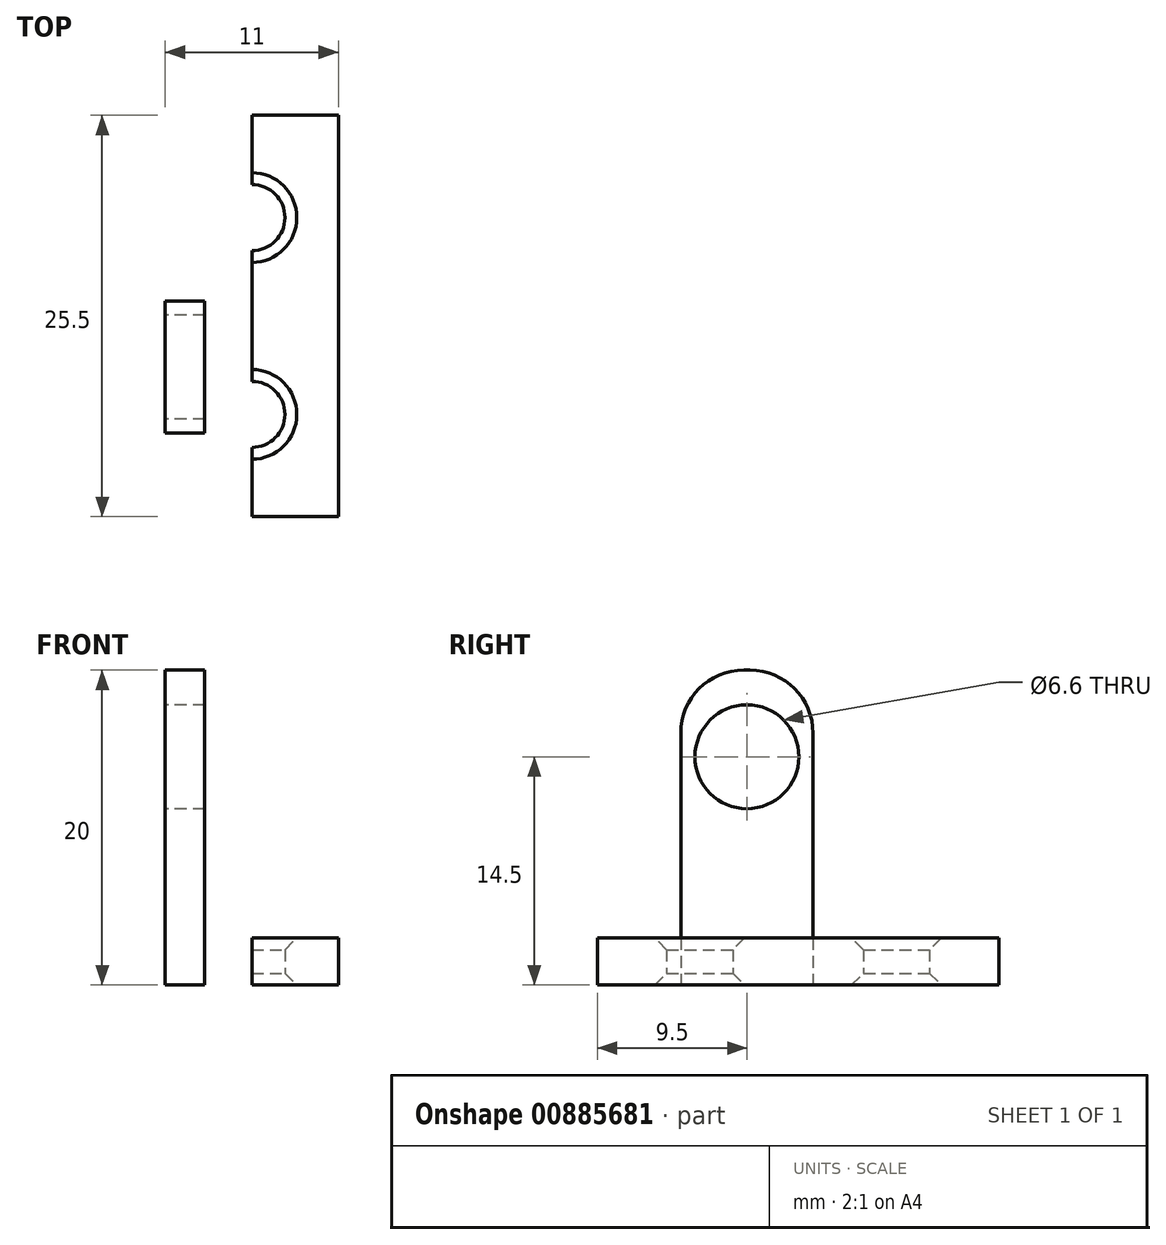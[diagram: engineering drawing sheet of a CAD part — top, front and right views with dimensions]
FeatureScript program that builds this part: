
annotation { "Feature Type Name" : "Feature", "Feature Type Description" : "" }
export const myFeature = defineFeature(function(context is Context, id is Id, definition is map)
    precondition{}
    {
        {
            var Q0;
            Q0=qCreatedBy(makeId("Top.planeOp"),FACE);
            var sketch = newSketch(context, id + "F0", { "sketchPlane" : qUnion([Q0])});
            skLineSegment(sketch, "E0.bottom", {"start": v(0, 0) * mm, "end": v(11, 0) * mm});
            skLineSegment(sketch, "E0.top", {"start": v(0, 25.5) * mm, "end": v(11, 25.5) * mm});
            skLineSegment(sketch, "E0.left", {"start": v(0, 0) * mm, "end": v(0, 25.5) * mm});
            skLineSegment(sketch, "E0.right", {"start": v(11, 0) * mm, "end": v(11, 25.5) * mm});
            skLineSegment(sketch, "E1", {"start": v(5.5, 0) * mm, "end": v(5.5, 25.5) * mm});
            skLineSegment(sketch, "E2", {"start": v(5.5, 0) * mm, "end": v(5.5, 6.5) * mm});
            skLineSegment(sketch, "E3", {"start": v(11, 12.75) * mm, "end": v(14.14, 12.75) * mm});
            skCircle(sketch, "E4", {"center": v(5.5, 6.5) * mm, "radius": 2.1 * mm});
            skCircle(sketch, "E5.MirrorC", {"center": v(5.5, 19) * mm, "radius": 2.1 * mm});
            skLineSegment(sketch, "E6", {"start": v(0, 0) * mm, "end": v(0, 9.5) * mm});
            skLineSegment(sketch, "E7", {"start": v(0, 9.5) * mm, "end": v(0, 5.3) * mm});
            skLineSegment(sketch, "E8", {"start": v(0, 9.5) * mm, "end": v(-2.03, 9.5) * mm});
            skLineSegment(sketch, "E9.MirrorCS", {"start": v(0, 9.5) * mm, "end": v(0, 13.7) * mm});
            skLineSegment(sketch, "E10", {"start": v(0, 5.3) * mm, "end": v(2.5, 5.3) * mm});
            skLineSegment(sketch, "E11.bottom", {"start": v(0, 13.7) * mm, "end": v(2.5, 13.7) * mm});
            skLineSegment(sketch, "E11.left", {"start": v(0, 13.7) * mm, "end": v(0, 5.3) * mm});
            skLineSegment(sketch, "E11.right", {"start": v(2.5, 13.7) * mm, "end": v(2.5, 5.3) * mm});
            skSolve(sketch);
        }
        {
            var Q0;
            {var subQ0=sQuery(id+"F0.wireOp",EDGE,"E0.right");var subQ3=makeQuery(id+"F0.imprint","IMPRINT",VERTEX,{"derivedFrom":subQ0});Q0=makeQuery(id+"F0.imprint","IMPRINT",FACE,{"disambiguationData":[TD([[makeQuery(id+"F0.imprint","IMPRINT",EDGE,{"disambiguationData":[TD([[subQ3,1.0]])],"derivedFrom":subQ0}),1.0]])]});}
            var Q1;
            {var subQ5=sQuery(id+"F0.wireOp",EDGE,"E0.left");Q1=makeQuery(id+"F0.imprint","IMPRINT",FACE,{"disambiguationData":[TD([[makeQuery(id+"F0.imprint","IMPRINT",EDGE,{"derivedFrom":subQ5}),-1.0]])]});}
            extrude(context, id + "F1", {"entities" : qUnion([Q0, Q1]), "depth" : 3 * mm, "offsetDistance" : 25 * mm});
        }
        {
            var Q0;
            {var subQ3=sQuery(id+"F0.wireOp",EDGE,"E11.bottom");Q0=makeQuery(id+"F0.imprint","IMPRINT",FACE,{"disambiguationData":[TD([[makeQuery(id+"F0.imprint","IMPRINT",EDGE,{"derivedFrom":subQ3}),-1.0]])]});}
            extrude(context, id + "F2", {"entities" : qUnion([Q0]), "operationType" : NewBodyOperationType.ADD, "depth" : 20 * mm, "offsetDistance" : 25 * mm});
        }
        {
            var Q0;
            Q0=qCreatedBy(makeId("Right.planeOp"),FACE);
            var sketch = newSketch(context, id + "F3", { "sketchPlane" : qUnion([Q0])});
            skLineSegment(sketch, "E12", {"start": v(0, 0) * mm, "end": v(9.5, 0) * mm});
            skLineSegment(sketch, "E13", {"start": v(9.5, 0) * mm, "end": v(9.5, 14.5) * mm});
            skCircle(sketch, "E14", {"center": v(9.5, 14.5) * mm, "radius": 3.3 * mm});
            skSolve(sketch);
        }
        {
            var Q0;
            Q0=makeQuery(id+"F3.imprint","IMPRINT",FACE,{"disambiguationData":[TD([[makeQuery(id+"F3.imprint","IMPRINT",EDGE,{"derivedFrom":sQuery(id+"F3.wireOp",EDGE,"E14")}),1.0]])]});
            extrude(context, id + "F4", {"entities" : qUnion([Q0]), "operationType" : NewBodyOperationType.REMOVE, "depth" : 25 * mm, "offsetDistance" : 25 * mm});
        }
        {
            var Q0;
            Q0=makeQuery(id+"F2.opExtrude","CAP_EDGE",EDGE,{"disambiguationData":[OSD([sQuery(id+"F0.wireOp",EDGE,"E10")])],"isStart":false});
            var Q1;
            Q1=makeQuery(id+"F2.opExtrude","CAP_EDGE",EDGE,{"disambiguationData":[OSD([sQuery(id+"F0.wireOp",EDGE,"E11.bottom")])],"isStart":false});
            fillet(context, id + "F5", {"entities" : qUnion([Q0, Q1]), "radius" : 4 * mm, "tangentPropagation" : true, "allowEdgeOverflow" : false});
        }
        {
            var Q0;
            Q0=makeQuery(id+"F1.opExtrude","CAP_EDGE",EDGE,{"disambiguationData":[OSD([sQuery(id+"F0.wireOp",EDGE,"E5.MirrorC")])],"isStart":false});
            var Q1;
            Q1=makeQuery(id+"F1.opExtrude","CAP_EDGE",EDGE,{"disambiguationData":[OSD([sQuery(id+"F0.wireOp",EDGE,"E5.MirrorC")])],"isStart":true});
            var Q2;
            Q2=makeQuery(id+"F1.opExtrude","CAP_EDGE",EDGE,{"disambiguationData":[OSD([sQuery(id+"F0.wireOp",EDGE,"E4")])],"isStart":true});
            var Q3;
            Q3=makeQuery(id+"F1.opExtrude","CAP_EDGE",EDGE,{"disambiguationData":[OSD([sQuery(id+"F0.wireOp",EDGE,"E4")])],"isStart":false});
            chamfer(context, id + "F6", {"entities" : qUnion([Q0, Q1, Q2, Q3]), "width" : .75 * mm, "tangentPropagation" : true});
        }
    });
